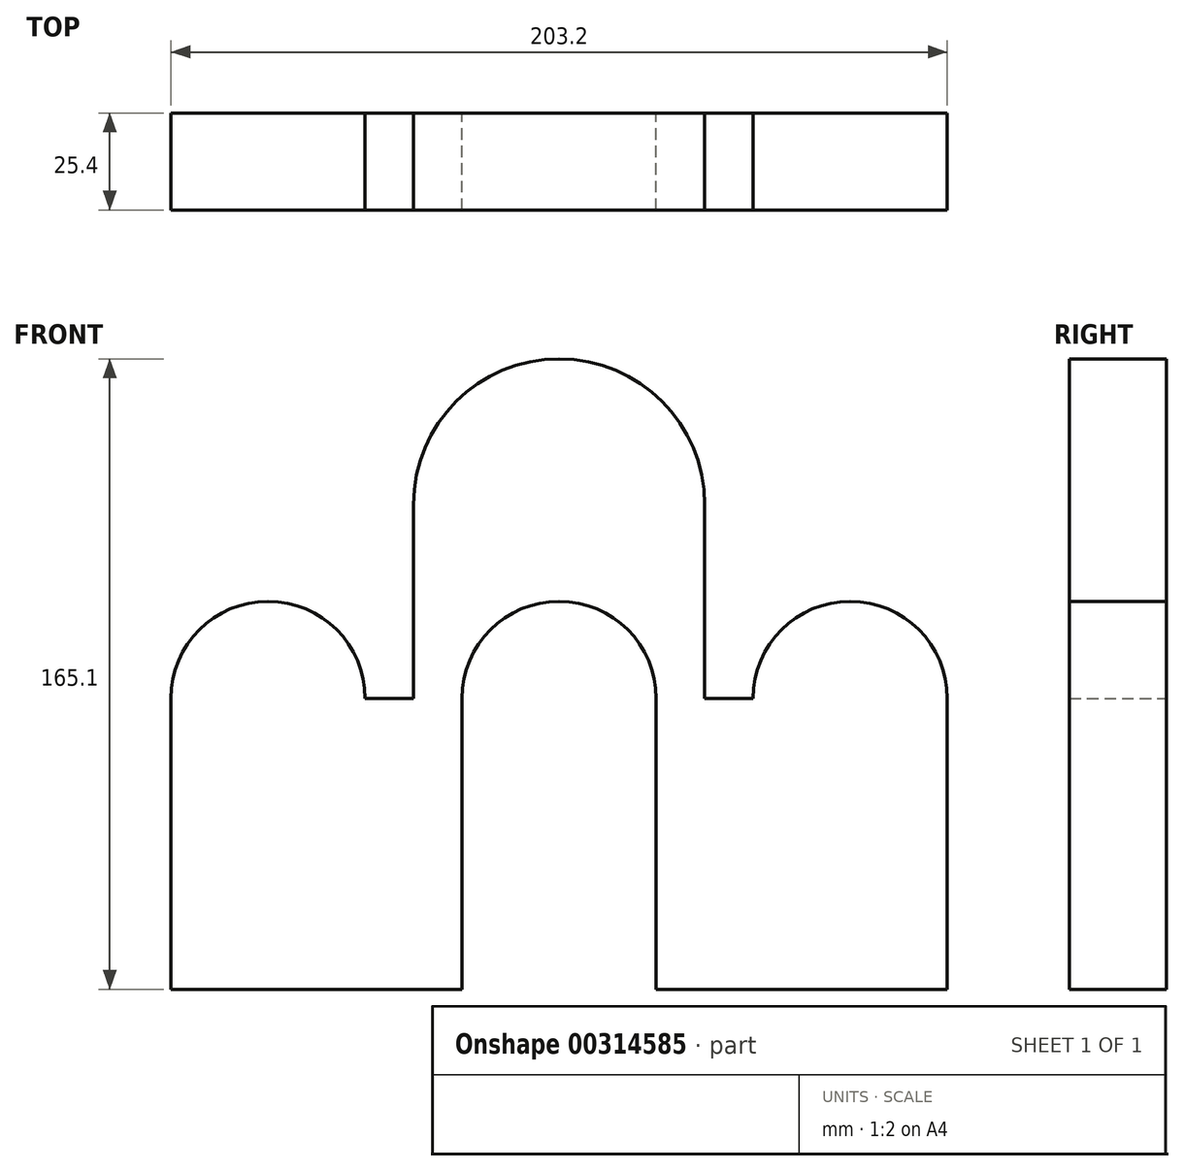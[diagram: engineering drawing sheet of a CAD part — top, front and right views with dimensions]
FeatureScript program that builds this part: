
annotation { "Feature Type Name" : "Feature", "Feature Type Description" : "" }
export const myFeature = defineFeature(function(context is Context, id is Id, definition is map)
    precondition{}
    {
        {
            var Q0;
            Q0=qCreatedBy(makeId("Front.planeOp"),FACE);
            var sketch = newSketch(context, id + "F0", { "sketchPlane" : qUnion([Q0])});
            skLineSegment(sketch, "E0", {"start": v(0, 0) * mm, "end": v(76.2, 0) * mm});
            skLineSegment(sketch, "E1", {"start": v(76.2, 0) * mm, "end": v(76.2, 76.2) * mm});
            skLineSegment(sketch, "E2", {"start": v(0, 0) * mm, "end": v(0, 76.2) * mm});
            skLineSegment(sketch, "E3", {"start": v(76.2, 0) * mm, "end": v(101.6, 0) * mm, "construction": true});
            skArc(sketch, "E4", {"start": v(0, 76.2) * mm, "mid": v(25.4, 101.6) * mm, "end": v(50.8, 76.2) * mm});
            skArc(sketch, "E5", {"start": v(76.2, 76.2) * mm, "mid": v(83.64, 94.16) * mm, "end": v(101.6, 101.6) * mm});
            skLineSegment(sketch, "E6", {"start": v(76.2, 76.2) * mm, "end": v(101.6, 76.2) * mm, "construction": true});
            skLineSegment(sketch, "E7", {"start": v(101.6, 76.2) * mm, "end": v(101.6, 101.6) * mm, "construction": true});
            skLineSegment(sketch, "E8", {"start": v(0, 76.2) * mm, "end": v(50.8, 76.2) * mm, "construction": true});
            skLineSegment(sketch, "E9", {"start": v(50.8, 76.2) * mm, "end": v(50.8, 76.2) * mm});
            skArc(sketch, "E10.MirrorCS", {"start": v(203.2, 76.2) * mm, "mid": v(177.8, 101.6) * mm, "end": v(152.4, 76.2) * mm});
            skLineSegment(sketch, "E11.MirrorCS", {"start": v(203.2, 0) * mm, "end": v(203.2, 76.2) * mm});
            skLineSegment(sketch, "E12.MirrorCS", {"start": v(203.2, 0) * mm, "end": v(127, 0) * mm});
            skLineSegment(sketch, "E13.MirrorCS", {"start": v(127, 0) * mm, "end": v(127, 76.2) * mm});
            skArc(sketch, "E14.MirrorCS", {"start": v(127, 76.2) * mm, "mid": v(119.56, 94.16) * mm, "end": v(101.6, 101.6) * mm});
            skLineSegment(sketch, "E15.MirrorCS", {"start": v(152.4, 76.2) * mm, "end": v(152.4, 76.2) * mm});
            skLineSegment(sketch, "E16", {"start": v(50.8, 76.2) * mm, "end": v(63.5, 76.2) * mm});
            skLineSegment(sketch, "E17", {"start": v(63.5, 76.2) * mm, "end": v(63.5, 127) * mm});
            skArc(sketch, "E18", {"start": v(63.5, 127) * mm, "mid": v(74.66, 153.94) * mm, "end": v(101.6, 165.1) * mm});
            skLineSegment(sketch, "E19", {"start": v(101.6, 165.1) * mm, "end": v(101.6, 127) * mm, "construction": true});
            skLineSegment(sketch, "E20", {"start": v(101.6, 127) * mm, "end": v(63.5, 127) * mm, "construction": true});
            skArc(sketch, "E21.MirrorCS", {"start": v(139.7, 127) * mm, "mid": v(128.54, 153.94) * mm, "end": v(101.6, 165.1) * mm});
            skLineSegment(sketch, "E22.MirrorCS", {"start": v(139.7, 76.2) * mm, "end": v(139.7, 127) * mm});
            skLineSegment(sketch, "E23.MirrorCS", {"start": v(152.4, 76.2) * mm, "end": v(139.7, 76.2) * mm});
            skSolve(sketch);
        }
        {
            var Q0;
            Q0=qCreatedBy(makeId("Front.planeOp"),FACE);
            var sketch = newSketch(context, id + "F1", { "sketchPlane" : qUnion([Q0])});
            skLineSegment(sketch, "E24", {"start": v(0, 0) * mm, "end": v(76.2, 0) * mm});
            skLineSegment(sketch, "E25", {"start": v(76.2, 0) * mm, "end": v(76.2, 76.2) * mm});
            skLineSegment(sketch, "E26", {"start": v(0, 0) * mm, "end": v(0, 76.2) * mm});
            skArc(sketch, "E27", {"start": v(0, 76.2) * mm, "mid": v(25.4, 101.6) * mm, "end": v(50.8, 76.2) * mm});
            skLineSegment(sketch, "E28", {"start": v(0, 76.2) * mm, "end": v(50.8, 76.2) * mm, "construction": true});
            skArc(sketch, "E29", {"start": v(76.2, 76.2) * mm, "mid": v(83.64, 94.16) * mm, "end": v(101.6, 101.6) * mm});
            skLineSegment(sketch, "E30", {"start": v(101.6, 76.2) * mm, "end": v(101.6, 114.12) * mm, "construction": true});
            skLineSegment(sketch, "E31", {"start": v(50.8, 76.2) * mm, "end": v(63.5, 76.2) * mm});
            skLineSegment(sketch, "E32", {"start": v(63.5, 76.2) * mm, "end": v(63.5, 127) * mm});
            skArc(sketch, "E33", {"start": v(63.5, 127) * mm, "mid": v(74.66, 153.94) * mm, "end": v(101.6, 165.1) * mm});
            skArc(sketch, "E34.MirrorCS", {"start": v(139.7, 127) * mm, "mid": v(128.54, 153.94) * mm, "end": v(101.6, 165.1) * mm});
            skLineSegment(sketch, "E35.MirrorCS", {"start": v(139.7, 76.2) * mm, "end": v(139.7, 127) * mm});
            skLineSegment(sketch, "E36.MirrorCS", {"start": v(152.4, 76.2) * mm, "end": v(139.7, 76.2) * mm});
            skArc(sketch, "E37.MirrorCS", {"start": v(203.2, 76.2) * mm, "mid": v(177.8, 101.6) * mm, "end": v(152.4, 76.2) * mm});
            skLineSegment(sketch, "E38.MirrorCS", {"start": v(203.2, 0) * mm, "end": v(203.2, 76.2) * mm});
            skLineSegment(sketch, "E39.MirrorCS", {"start": v(203.2, 0) * mm, "end": v(127, 0) * mm});
            skLineSegment(sketch, "E40.MirrorCS", {"start": v(127, 0) * mm, "end": v(127, 76.2) * mm});
            skArc(sketch, "E41.MirrorCS", {"start": v(127, 76.2) * mm, "mid": v(119.56, 94.16) * mm, "end": v(101.6, 101.6) * mm});
            skSolve(sketch);
        }
        {
            var Q0;
            Q0 = qSketchRegion(id + "F1", true);
            extrude(context, id + "F2", {"entities" : qUnion([Q0]), "depth" : 25.4 * mm});
        }
    });
